# Revit family: Im-Beton-Kanalsystem_IBK_Verbindungselement_48_mm
name_source: partatom
category: Generic Models
revit_build: Autodesk Revit 2015 (Build: 20140606_1530(x64)
units: mm (PartAtom-declared; Revit-internal decimal feet)

## types (2) — shared parameters
Height = 48 mm  [stored 0.15748 ft]
Manufacturer = OBO Bettermann
Material = Steel, Galvanized
URL = http://www.obo-bettermann.com

## per-type parameters (varying)
| type | GTIN | Manufacturer Art. No. | Outer width | Width | Width 2 |
| IBVE 35048 | 4012196331864
4012196331864 | 7399898 | 428 mm  [stored 1.4042 ft] | 350 mm  [stored 1.14829 ft] | 357 mm |
| IBVE 25048 | 4012196331840 | 7399892 | 328 mm  [stored 1.07612 ft] | 250 mm  [stored 0.82021 ft] | 257 mm  [stored 0.843176 ft] |

note: column(s) folded — value = type name in every type: Article Type

note: [stored X ft] marks values corroborated as IEEE doubles in the binary element streams (Revit-internal decimal feet)

## geometry (parser evidence)
native form markers: Sweep x2
no freeform markers — native parametric forms only
